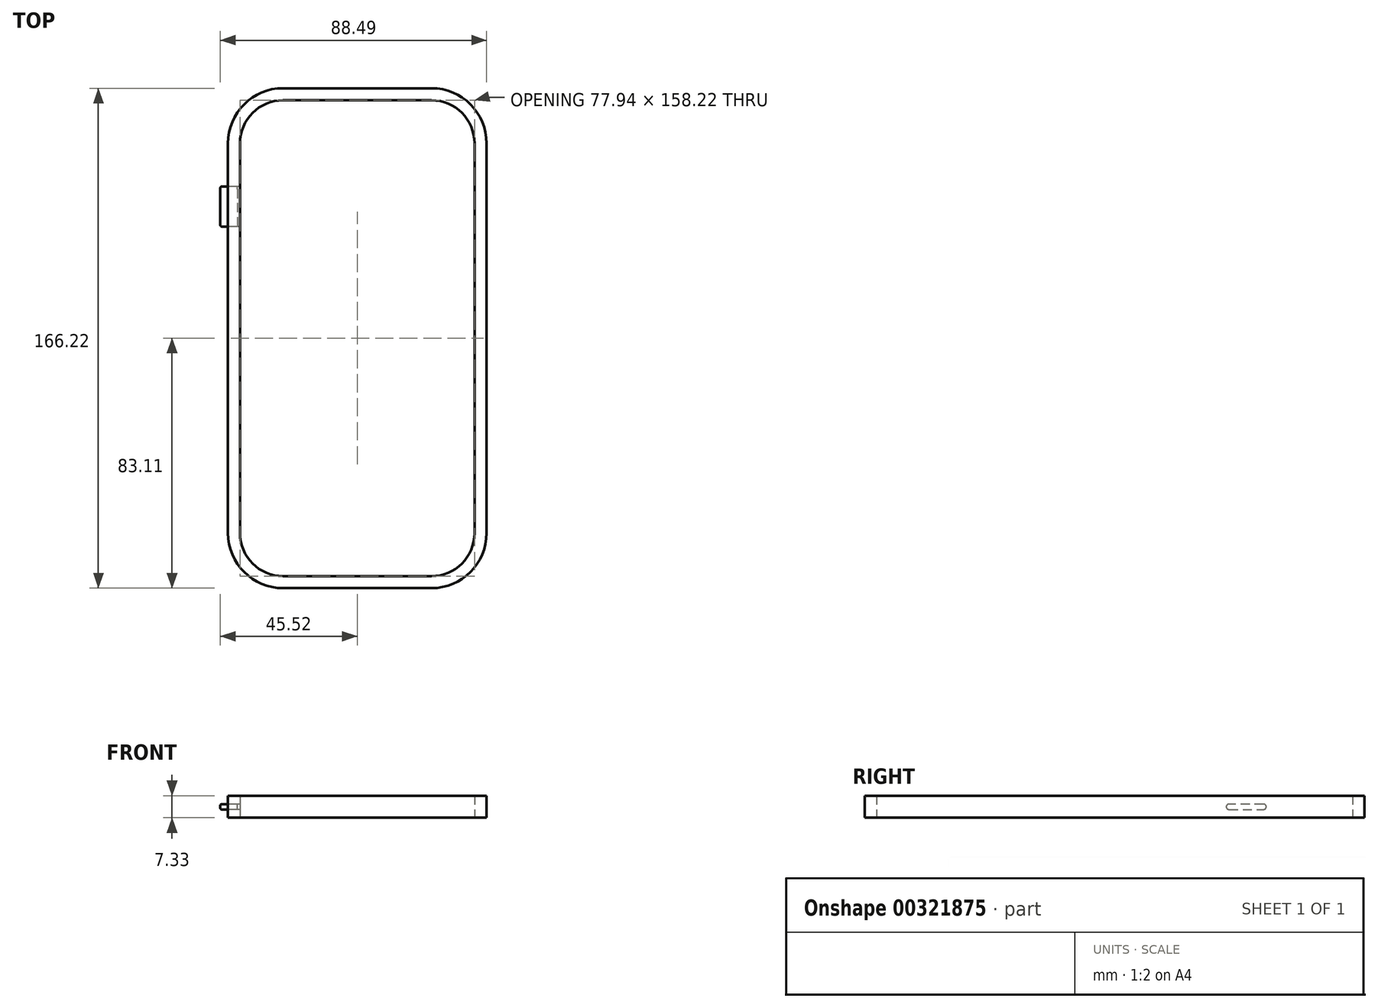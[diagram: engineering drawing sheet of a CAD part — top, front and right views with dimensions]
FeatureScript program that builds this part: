
annotation { "Feature Type Name" : "Feature", "Feature Type Description" : "" }
export const myFeature = defineFeature(function(context is Context, id is Id, definition is map)
    precondition{}
    {
        {
            var Q0;
            Q0=qCreatedBy(makeId("Top.planeOp"),FACE);
            var sketch = newSketch(context, id + "F0", { "sketchPlane" : qUnion([Q0])});
            skLineSegment(sketch, "E0.bottom", {"start": v(-24.67, 79.11) * mm, "end": v(24.67, 79.11) * mm});
            skLineSegment(sketch, "E0.top", {"start": v(-24.67, -79.1) * mm, "end": v(24.67, -79.1) * mm});
            skLineSegment(sketch, "E0.left", {"start": v(-38.97, 64.81) * mm, "end": v(-38.97, -64.8) * mm});
            skLineSegment(sketch, "E0.right", {"start": v(38.97, 64.81) * mm, "end": v(38.97, -64.8) * mm});
            skPoint(sketch, "E0.middle", {"position": v(0, 0) * mm});
            skPoint(sketch, "E1.visualSharp", {"position": v(-38.97, 79.11) * mm});
            skArc(sketch, "E1.filletArc", {"start": v(-24.67, 79.11) * mm, "mid": v(-34.78, 74.92) * mm, "end": v(-38.97, 64.81) * mm});
            skPoint(sketch, "E2.visualSharp", {"position": v(38.97, 79.11) * mm});
            skArc(sketch, "E2.filletArc", {"start": v(38.97, 64.81) * mm, "mid": v(34.78, 74.92) * mm, "end": v(24.67, 79.11) * mm});
            skPoint(sketch, "E3.visualSharp", {"position": v(38.97, -79.1) * mm});
            skArc(sketch, "E3.filletArc", {"start": v(24.67, -79.1) * mm, "mid": v(34.78, -74.92) * mm, "end": v(38.97, -64.8) * mm});
            skPoint(sketch, "E4.visualSharp", {"position": v(-38.97, -79.1) * mm});
            skArc(sketch, "E4.filletArc", {"start": v(-38.97, -64.8) * mm, "mid": v(-34.78, -74.92) * mm, "end": v(-24.67, -79.1) * mm});
            skLineSegment(sketch, "E5.0", {"start": v(-24.67, 83.11) * mm, "end": v(24.67, 83.11) * mm});
            skArc(sketch, "E5.1", {"start": v(42.97, 64.81) * mm, "mid": v(37.61, 77.75) * mm, "end": v(24.67, 83.11) * mm});
            skArc(sketch, "E5.2", {"start": v(-24.67, 83.11) * mm, "mid": v(-37.61, 77.75) * mm, "end": v(-42.97, 64.81) * mm});
            skLineSegment(sketch, "E5.3", {"start": v(42.97, 64.81) * mm, "end": v(42.97, -64.8) * mm});
            skLineSegment(sketch, "E5.4", {"start": v(-42.97, 64.81) * mm, "end": v(-42.97, -64.8) * mm});
            skArc(sketch, "E5.5", {"start": v(-42.97, -64.8) * mm, "mid": v(-37.61, -77.75) * mm, "end": v(-24.67, -83.11) * mm});
            skLineSegment(sketch, "E5.6", {"start": v(-24.67, -83.11) * mm, "end": v(24.67, -83.11) * mm});
            skArc(sketch, "E5.7", {"start": v(24.67, -83.11) * mm, "mid": v(37.61, -77.75) * mm, "end": v(42.97, -64.8) * mm});
            skLineSegment(sketch, "E6", {"start": v(-17.54, 79.11) * mm, "end": v(-17.54, 43.63) * mm});
            skLineSegment(sketch, "E7", {"start": v(-17.54, 43.63) * mm, "end": v(-80.07, 43.63) * mm});
            skSolve(sketch);
        }
        {
            var Q0;
            Q0=makeQuery(id+"F0.imprint","IMPRINT",FACE,{"disambiguationData":[TD([[makeQuery(id+"F0.imprint","IMPRINT",EDGE,{"derivedFrom":sQuery(id+"F0.wireOp",EDGE,"E0.bottom")}),1.0]])]});
            extrude(context, id + "F1", {"entities" : qUnion([Q0]), "depth" : 7.33 * mm});
        }
        {
            var Q0;
            Q0=makeQuery(id+"F1.opExtrude","SWEPT_FACE",FACE,{"disambiguationData":[OSD([sQuery(id+"F0.wireOp",EDGE,"E5.4")])]});
            cPlane(context, id + "F2", {"entities" : qUnion([Q0]), "cplaneType" : CPlaneType.OFFSET, "offset" : 0 * mm, "width" : 150 * mm, "height" : 150 * mm});
        }
        {
            var Q0;
            Q0=qCreatedBy(id+"F2.planeOp",FACE);
            var sketch = newSketch(context, id + "F3", { "sketchPlane" : qUnion([Q0])});
            skPoint(sketch, "E8.start.orphan", {"position": v(-43.77, 7.37) * mm});
            skPoint(sketch, "E9.end.orphan", {"position": v(-43.77, 3.65) * mm});
            skPoint(sketch, "E9.start.orphan", {"position": v(-43.77, 0) * mm});
            skLineSegment(sketch, "E10", {"start": v(-43.77, 2.75) * mm, "end": v(-49.5, 2.75) * mm});
            skLineSegment(sketch, "E11", {"start": v(-49.5, 2.75) * mm, "end": v(-43.77, 2.75) * mm});
            skLineSegment(sketch, "E12.MirrorCS", {"start": v(-49.5, 4.55) * mm, "end": v(-43.77, 4.55) * mm});
            skArc(sketch, "E13", {"start": v(-49.5, 4.55) * mm, "mid": v(-50.41, 3.65) * mm, "end": v(-49.5, 2.75) * mm});
            skLineSegment(sketch, "E14.MirrorCS", {"start": v(-38.03, 2.75) * mm, "end": v(-43.77, 2.75) * mm});
            skArc(sketch, "E15.MirrorCS", {"start": v(-38.03, 4.55) * mm, "mid": v(-37.13, 3.65) * mm, "end": v(-38.03, 2.75) * mm});
            skLineSegment(sketch, "E16.MirrorCS", {"start": v(-38.03, 4.55) * mm, "end": v(-43.77, 4.55) * mm});
            skSolve(sketch);
        }
        {
            var Q0;
            Q0 = qSketchRegion(id + "F3", true);
            extrude(context, id + "F4", {"entities" : qUnion([Q0]), "operationType" : NewBodyOperationType.ADD, "depth" : 2.55 * mm});
        }
        {
            var Q0;
            Q0=makeQuery(id+"F4.opExtrude","CAP_EDGE",EDGE,{"disambiguationData":[OSD([sQuery(id+"F3.wireOp",EDGE,"E11"),sQuery(id+"F3.wireOp",EDGE,"E14.MirrorCS")])],"isStart":false});
            var Q1;
            Q1=makeQuery(id+"F4.opExtrude","CAP_EDGE",EDGE,{"disambiguationData":[OSD([sQuery(id+"F3.wireOp",EDGE,"E12.MirrorCS"),sQuery(id+"F3.wireOp",EDGE,"E16.MirrorCS")])],"isStart":false});
            var Q2;
            Q2=makeQuery(id+"F4.opExtrude","CAP_EDGE",EDGE,{"disambiguationData":[OSD([sQuery(id+"F3.wireOp",EDGE,"E15.MirrorCS")])],"isStart":false});
            var Q3;
            Q3=makeQuery(id+"F4.opExtrude","CAP_EDGE",EDGE,{"disambiguationData":[OSD([sQuery(id+"F3.wireOp",EDGE,"E13")])],"isStart":false});
            fillet(context, id + "F5", {"entities" : qUnion([Q0, Q1, Q2, Q3]), "radius" : .5 * mm, "tangentPropagation" : true, "allowEdgeOverflow" : false});
        }
        {
            var Q0;
            Q0 = qSketchRegion(id + "F3", true);
            extrude(context, id + "F6", {"entities" : qUnion([Q0]), "operationType" : NewBodyOperationType.REMOVE, "oppositeDirection" : true, "depth" : 5 * mm});
        }
        {
            var Q0;
            Q0=makeQuery(id+"F6.boolean.opBoolean","COPY",FACE,{"derivedFrom":makeQuery(id+"F6.opExtrude","CAP_FACE",FACE,{"disambiguationData":[OSD([sQuery(id+"F3.wireOp",EDGE,"E11"),sQuery(id+"F3.wireOp",EDGE,"E12.MirrorCS"),sQuery(id+"F3.wireOp",EDGE,"E13"),sQuery(id+"F3.wireOp",EDGE,"E14.MirrorCS"),sQuery(id+"F3.wireOp",EDGE,"E15.MirrorCS"),sQuery(id+"F3.wireOp",EDGE,"E16.MirrorCS")])],"isStart":true})});
            extrude(context, id + "F7", {"entities" : qUnion([Q0]), "depth" : 3.14 * mm});
        }
    });
